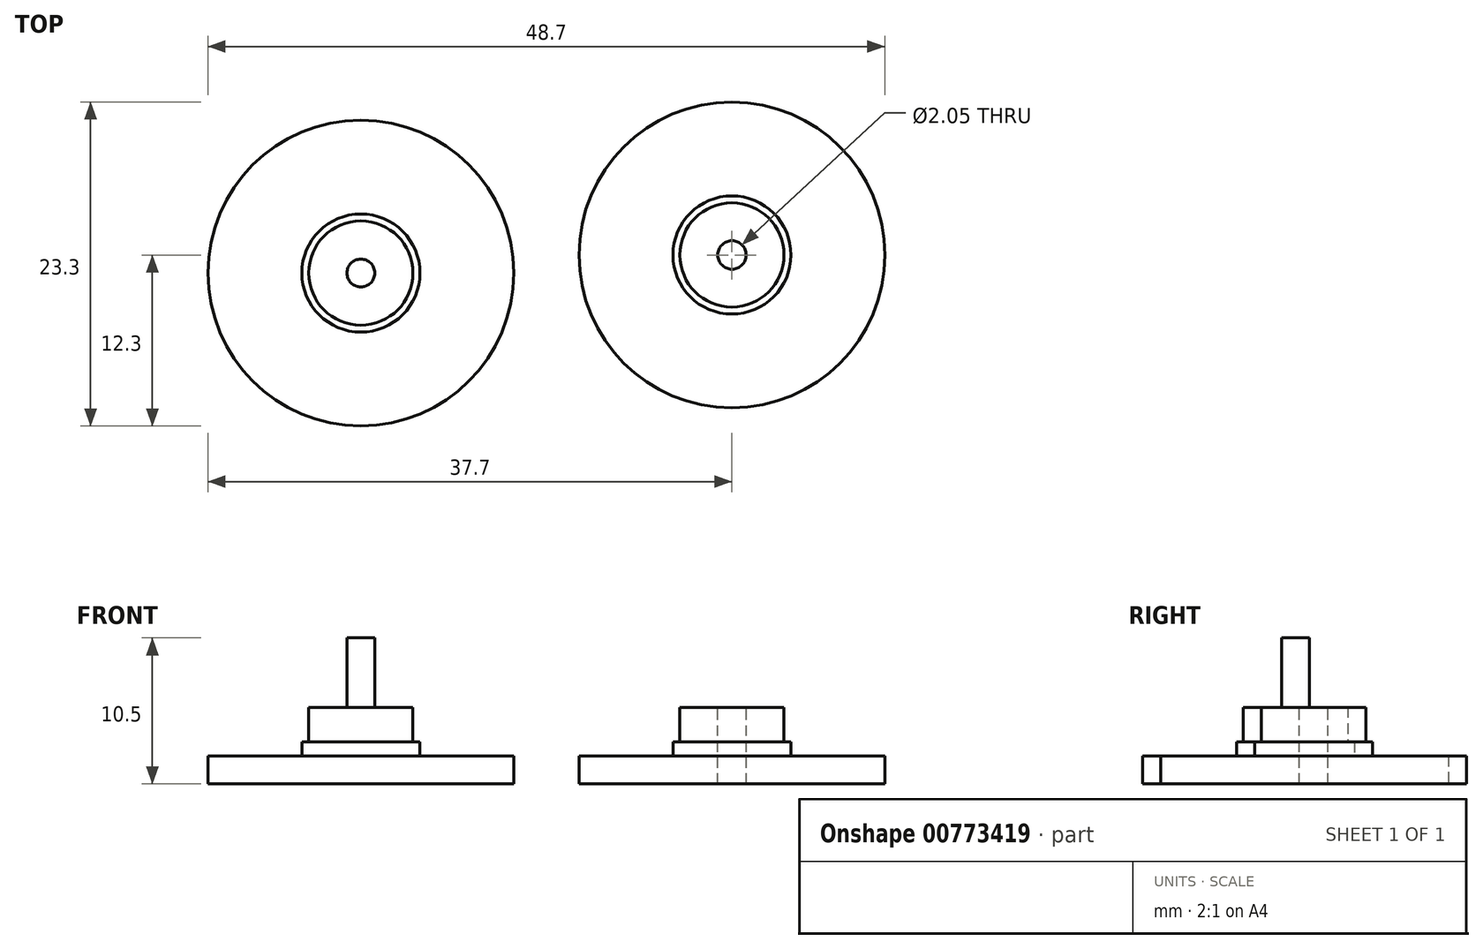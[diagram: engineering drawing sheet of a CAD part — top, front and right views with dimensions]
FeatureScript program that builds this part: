
annotation { "Feature Type Name" : "Feature", "Feature Type Description" : "" }
export const myFeature = defineFeature(function(context is Context, id is Id, definition is map)
    precondition{}
    {
        {
            var Q0;
            Q0=qCreatedBy(makeId("Top.planeOp"),FACE);
            var sketch = newSketch(context, id + "F0", { "sketchPlane" : qUnion([Q0])});
            skCircle(sketch, "E0", {"center": v(0, 0) * mm, "radius": 3.75 * mm});
            skCircle(sketch, "E1", {"center": v(0, 0) * mm, "radius": 4.25 * mm});
            skCircle(sketch, "E2", {"center": v(0, 0) * mm, "radius": 11 * mm});
            skSolve(sketch);
        }
        {
            var Q0;
            Q0=makeQuery(id+"F0.imprint","IMPRINT",FACE,{"disambiguationData":[TD([[makeQuery(id+"F0.imprint","IMPRINT",EDGE,{"derivedFrom":sQuery(id+"F0.wireOp",EDGE,"E0")}),1.0]])]});
            extrude(context, id + "F1", {"entities" : qUnion([Q0]), "depth" : 5.5 * mm});
        }
        {
            var Q0;
            Q0=makeQuery(id+"F0.imprint","IMPRINT",FACE,{"disambiguationData":[TD([[makeQuery(id+"F0.imprint","IMPRINT",EDGE,{"derivedFrom":sQuery(id+"F0.wireOp",EDGE,"E0")}),-1.0]])]});
            extrude(context, id + "F2", {"entities" : qUnion([Q0]), "operationType" : NewBodyOperationType.ADD, "depth" : 3 * mm, "offsetDistance" : 25 * mm});
        }
        {
            var Q0;
            Q0=makeQuery(id+"F0.imprint","IMPRINT",FACE,{"disambiguationData":[TD([[makeQuery(id+"F0.imprint","IMPRINT",EDGE,{"derivedFrom":sQuery(id+"F0.wireOp",EDGE,"E1")}),-1.0]])]});
            extrude(context, id + "F3", {"entities" : qUnion([Q0]), "operationType" : NewBodyOperationType.ADD, "depth" : 2 * mm});
        }
        {
            var Q0;
            Q0=makeQuery(id+"F1.opExtrude","SWEPT_BODY",BODY,{"disambiguationData":[OSD([sQuery(id+"F0.wireOp",EDGE,"E0")])]});
            transform(context, id + "F4", {"entities" : qUnion([Q0]), "transformType" : TransformType.TRANSLATION_3D, "dx" : 26.7 * mm, "dy" : 1.3 * mm, "dz" : 0 * mm, "makeCopy" : true});
        }
        {
            var Q0;
            Q0=makeQuery(id+"F1.opExtrude","CAP_FACE",FACE,{"disambiguationData":[OSD([sQuery(id+"F0.wireOp",EDGE,"E0")])],"isStart":false});
            var sketch = newSketch(context, id + "F5", { "sketchPlane" : qUnion([Q0])});
            skCircle(sketch, "E3", {"center": v(0, 0) * mm, "radius": 1 * mm});
            skSolve(sketch);
        }
        {
            var Q0;
            Q0=makeQuery(id+"F5.imprint","IMPRINT",FACE,{"disambiguationData":[TD([[makeQuery(id+"F5.imprint","IMPRINT",EDGE,{"derivedFrom":sQuery(id+"F5.wireOp",EDGE,"E3")}),1.0]])]});
            extrude(context, id + "F6", {"entities" : qUnion([Q0]), "operationType" : NewBodyOperationType.ADD, "depth" : 5 * mm});
        }
        {
            var Q0;
            Q0=makeQuery(id+"F4.opPattern","COPY",FACE,{"derivedFrom":makeQuery(id+"F1.opExtrude","CAP_FACE",FACE,{"disambiguationData":[OSD([sQuery(id+"F0.wireOp",EDGE,"E0")])],"isStart":false}),"instanceName":"1"});
            var sketch = newSketch(context, id + "F7", { "sketchPlane" : qUnion([Q0])});
            skCircle(sketch, "E4", {"center": v(26.7, 1.3) * mm, "radius": 1.02 * mm});
            skSolve(sketch);
        }
        {
            var Q0;
            Q0=makeQuery(id+"F7.imprint","IMPRINT",FACE,{"disambiguationData":[TD([[makeQuery(id+"F7.imprint","IMPRINT",EDGE,{"derivedFrom":sQuery(id+"F7.wireOp",EDGE,"E4")}),1.0]])]});
            extrude(context, id + "F8", {"entities" : qUnion([Q0]), "operationType" : NewBodyOperationType.REMOVE, "oppositeDirection" : true, "depth" : 7.7 * mm});
        }
    });
